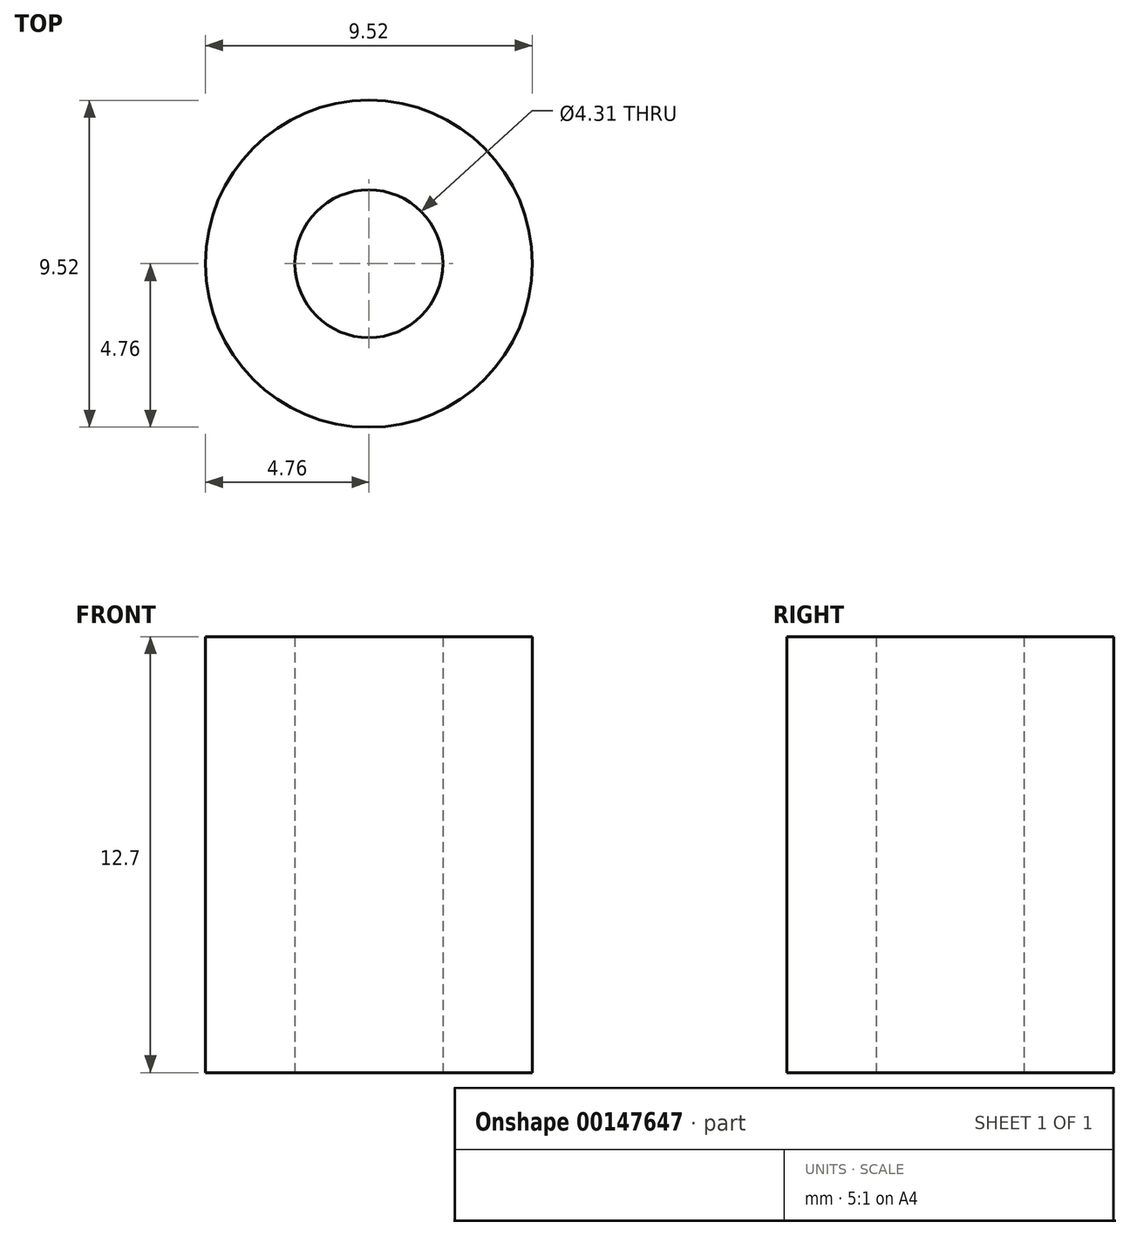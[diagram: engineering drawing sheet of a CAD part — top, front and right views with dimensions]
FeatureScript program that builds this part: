
annotation { "Feature Type Name" : "Feature", "Feature Type Description" : "" }
export const myFeature = defineFeature(function(context is Context, id is Id, definition is map)
    precondition{}
    {
        {
            var Q0;
            Q0=qCreatedBy(makeId("Top.planeOp"),FACE);
            var sketch = newSketch(context, id + "F0", { "sketchPlane" : qUnion([Q0])});
            skCircle(sketch, "E0", {"center": v(0, 0) * mm, "radius": 4.76 * mm});
            skCircle(sketch, "E1", {"center": v(0, 0) * mm, "radius": 2.15 * mm});
            skSolve(sketch);
        }
        {
            var Q0;
            Q0=qSketchRegion(id+"F0",true);
            extrude(context, id + "F1", {"entities" : qUnion([Q0]), "depth" : 12.7 * mm});
        }
    });
